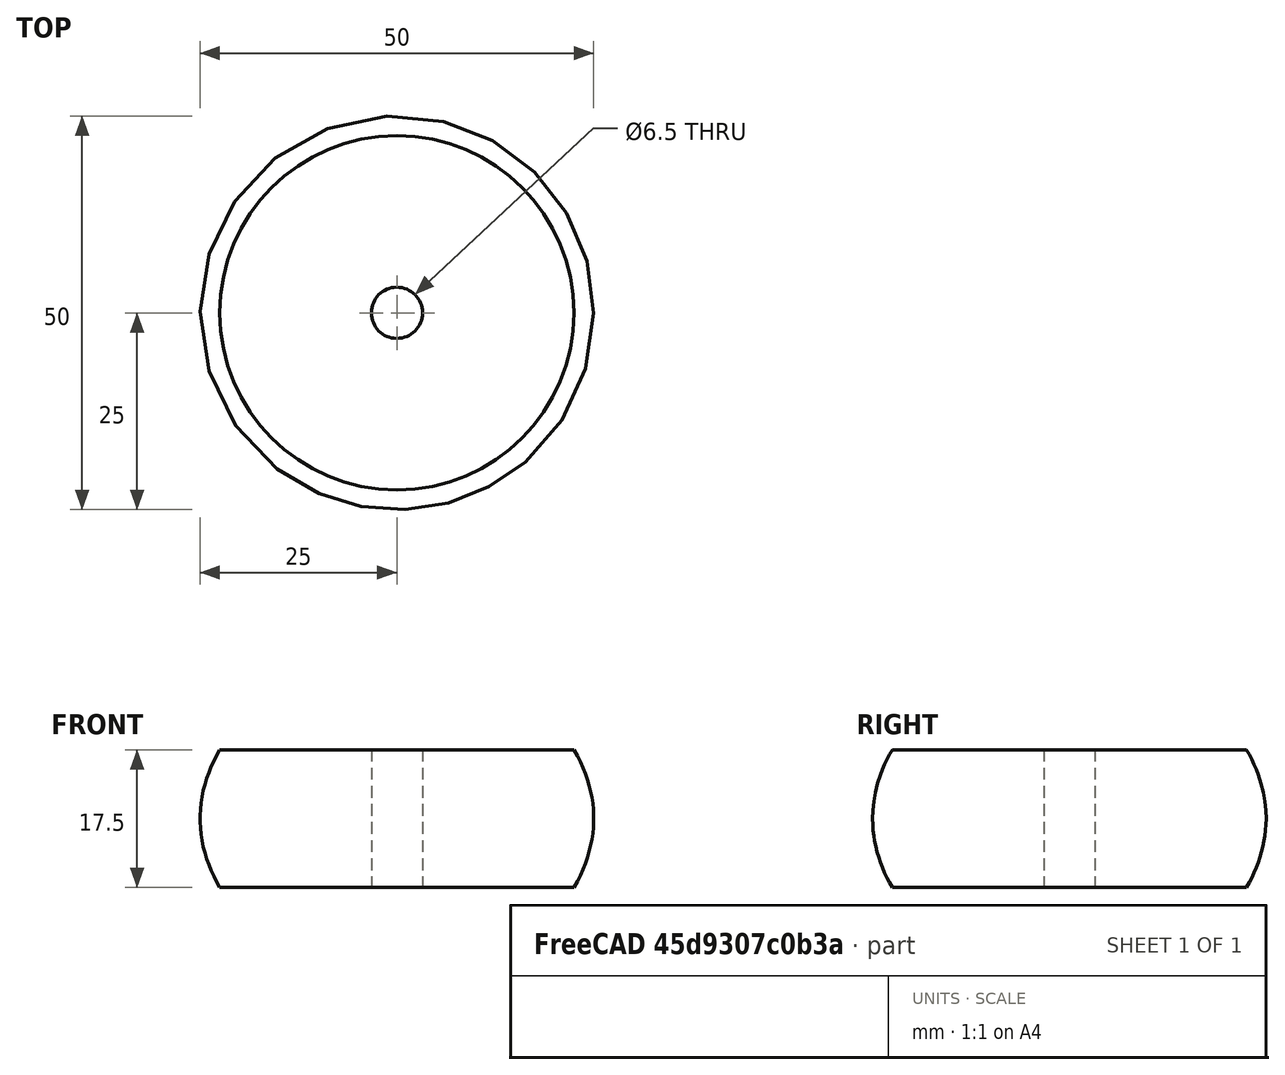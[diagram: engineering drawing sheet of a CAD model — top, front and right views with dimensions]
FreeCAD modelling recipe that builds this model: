
FCSTD DOCUMENT  (FreeCAD 1.0R39109 (Git))
Label: luggage_wheel
License: All rights reserved
LicenseURL: https://en.wikipedia.org/wiki/All_rights_reserved
objects: Sketcher::SketchObject×1, PartDesign::Revolution×1, PartDesign::Body×1
note: 6 computed .brp shape members not serialized (recipe doc carries the construction recipe); baked Part::Feature solids carry a one-line shape summary decoded from their .brp

FEATURE [Sketcher::SketchObject] Sketch  label="Profile"
  ArcFitTolerance = 0
  AttachmentSupport = -> [XZ_Plane]
  FullyConstrained = true
  MakeInternals = false
  MapMode = 5
  Placement = pos=(0,0,0) rot=(1,0,0;1.5708rad)
  sketch-geometry (28):
    g0: LineSegment [constr] StartX=-25 StartY=-8.75 StartZ=0 EndX=-25 EndY=8.75 EndZ=0
    g1: LineSegment [constr] StartX=-25 StartY=8.75 StartZ=0 EndX=25 EndY=8.75 EndZ=0
    g2: LineSegment [constr] StartX=25 StartY=8.75 StartZ=0 EndX=25 EndY=-8.75 EndZ=0
    g3: LineSegment [constr] StartX=25 StartY=-8.75 StartZ=0 EndX=-25 EndY=-8.75 EndZ=0
    g4: GeomPoint [constr] X=0 Y=0 Z=0
    g5: LineSegment [constr] StartX=-3.25 StartY=-8.75 StartZ=0 EndX=-3.25 EndY=8.75 EndZ=0
    g6: LineSegment [constr] StartX=-3.25 StartY=8.75 StartZ=0 EndX=3.25 EndY=8.75 EndZ=0
    g7: LineSegment [constr] StartX=3.25 StartY=8.75 StartZ=0 EndX=3.25 EndY=-8.75 EndZ=0
    g8: LineSegment [constr] StartX=3.25 StartY=-8.75 StartZ=0 EndX=-3.25 EndY=-8.75 EndZ=0
    g9: GeomPoint [constr] X=0 Y=0 Z=0
    g10: Circle [constr] CenterX=-22.5 CenterY=8.75 CenterZ=0 NormalX=0 NormalY=0 NormalZ=1 AngleXU=0 Radius=1
    g11: Circle [constr] CenterX=-27.5 CenterY=0 CenterZ=0 NormalX=0 NormalY=0 NormalZ=1 AngleXU=0 Radius=1
    g12: Circle [constr] CenterX=-22.5 CenterY=-8.75 CenterZ=0 NormalX=0 NormalY=0 NormalZ=1 AngleXU=0 Radius=1
    g13: BSplineCurve PolesCount=3 KnotsCount=2 Degree=2 IsPeriodic=0
    g14: GeomPoint [constr] X=-22.5 Y=8.75 Z=0
    g15: GeomPoint [constr] X=-22.5 Y=-8.75 Z=0
    g16: Circle [constr] CenterX=22.5 CenterY=-8.75 CenterZ=0 NormalX=0 NormalY=0 NormalZ=1 AngleXU=0 Radius=1
    g17: Circle [constr] CenterX=27.5 CenterY=0 CenterZ=0 NormalX=0 NormalY=0 NormalZ=1 AngleXU=0 Radius=1
    g18: Circle [constr] CenterX=22.5 CenterY=8.75 CenterZ=0 NormalX=0 NormalY=0 NormalZ=1 AngleXU=0 Radius=1
    g19: BSplineCurve PolesCount=3 KnotsCount=2 Degree=2 IsPeriodic=0
    g20: GeomPoint [constr] X=22.5 Y=-8.75 Z=0
    g21: GeomPoint [constr] X=22.5 Y=8.75 Z=0
    g22: LineSegment StartX=-22.5 StartY=8.75 StartZ=0 EndX=-3.25 EndY=8.75 EndZ=0
    g23: LineSegment StartX=-3.25 StartY=8.75 StartZ=0 EndX=-3.25 EndY=-8.75 EndZ=0
    g24: LineSegment StartX=-3.25 StartY=-8.75 StartZ=0 EndX=-22.5 EndY=-8.75 EndZ=0
    g25: LineSegment StartX=22.5 StartY=8.75 StartZ=0 EndX=3.25 EndY=8.75 EndZ=0
    g26: LineSegment StartX=3.25 StartY=8.75 StartZ=0 EndX=3.25 EndY=-8.75 EndZ=0
    g27: LineSegment StartX=3.25 StartY=-8.75 StartZ=0 EndX=22.5 EndY=-8.75 EndZ=0
  constraints (62):
    c: Coincident(g0,g1)
    c: Coincident(g1,g2)
    c: Coincident(g2,g3)
    c: Coincident(g3,g0)
    c: Horizontal(g1)
    c: Horizontal(g3)
    c: Vertical(g0)
    c: Vertical(g2)
    c: Symmetric(g1,g0,g4)
    c: Coincident(g4,g-1)
    c: DistanceX(g1,g1) = 50  'outer_diameter'
    c: DistanceY(g2,g2) = 17.5  'width'
    c: Coincident(g5,g6)
    c: Coincident(g6,g7)
    c: Coincident(g7,g8)
    c: Coincident(g8,g5)
    c: Horizontal(g6)
    c: Horizontal(g8)
    c: Vertical(g5)
    c: Vertical(g7)
    c: Symmetric(g6,g5,g9)
    c: Coincident(g9,g4)
    c: DistanceX(g5,g6) = 6.5  'shaft_diameter'
    c: Weight(g10) = 1
    c: PointOnObject(g13,g1)
    c: Equal(g10,g11)
    c: PointOnObject(g11,g-1)
    c: Equal(g10,g12)
    c: PointOnObject(g13,g3)
    c: InternalAlignment(g10,g13)
    c: InternalAlignment(g11,g13)
    c: InternalAlignment(g12,g13)
    c: InternalAlignment(g14,g13)
    c: InternalAlignment(g15,g13)
    c: Vertical(g13,g13)
    c: Weight(g16) = 1
    c: Equal(g16,g17)
    c: Equal(g16,g18)
    c: PointOnObject(g19,g1)
    c: InternalAlignment(g16,g19)
    c: InternalAlignment(g17,g19)
    c: InternalAlignment(g18,g19)
    c: InternalAlignment(g20,g19)
    c: InternalAlignment(g21,g19)
    c: Vertical(g19,g19)
    c: Symmetric(g13,g19,g-2)
    c: DistanceX(g13,g19) = 45
    c: DistanceX(g11,g17) = 55
    c: Symmetric(g17,g11,g-2)
    c: Coincident(g22,g13)
    c: Coincident(g22,g5)
    c: Coincident(g22,g23)
    c: Coincident(g23,g5)
    c: Coincident(g23,g24)
    c: Coincident(g24,g13)
    c: Coincident(g25,g19)
    c: Coincident(g25,g6)
    c: Horizontal(g25)
    c: Coincident(g25,g26)
    c: Coincident(g26,g7)
    c: Coincident(g26,g27)
    c: Coincident(g27,g19)
FEATURE [PartDesign::Revolution] Revolution
  Angle = 360
  Angle2 = 60
  Axis = (0,2e-16,1)
  Base = (0,0,0)
  Placement = pos=(0,0,0) rot=(1,0,0;1.5708rad)
  Profile = -> Sketch
  ReferenceAxis = -> Sketch [V_Axis]
  Suppressed = false
  Type = 0
FEATURE [PartDesign::Body] Body
  AllowCompound = false
  Group = -> [Sketch,Revolution]
  Origin = -> Origin
  Tip = -> Revolution
